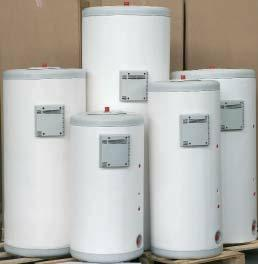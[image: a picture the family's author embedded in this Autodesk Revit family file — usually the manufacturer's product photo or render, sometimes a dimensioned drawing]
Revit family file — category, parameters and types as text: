
# Revit family: CV-80-M1S_CC01701
name_source: partatom
category: Aparatos eléctricos
revit_build: Autodesk Revit 2016 (Build: 20150220_1215(x64)
units: mm (PartAtom-declared; Revit-internal decimal feet)

## family parameters
Compartido = No
Corte con vacíos al cargar = No
Número OmniClass = 23.80.00.00
Punto de cálculo de habitación = No
Se basa en plano de trabajo = No
Siempre vertical = Sí
Título OmniClass = Electric Power and Lighting

## types (1)
- Interacumuladores CV-M1S
    Clase eficiencia energética = B
    Costo = 0 $
    Código de montaje = CC01701
    Descripción = INTERACUMULADOR CON SERPENTIN FIJO
    Dimensiones = 480 x 935 mm
    Fabricante = SALVADOR ESCODA
    Imagen de tipo = CV-M1S.jpg
    Modelo = CV 80 M1S
    Peso vacío (aprox.) = 40 Kg
    Presión máx. depósito = 8 bar
    Pérdidas estáticas = 46 W
    Superfície intercambiador = 0,3 m2
    Temperatura máx. ACS = 90 ºC
    Temperatura máx. circuito calentamiento = 200 ºC
    URL = www.salvadorescoda.com
    Volúmen = 80 l
